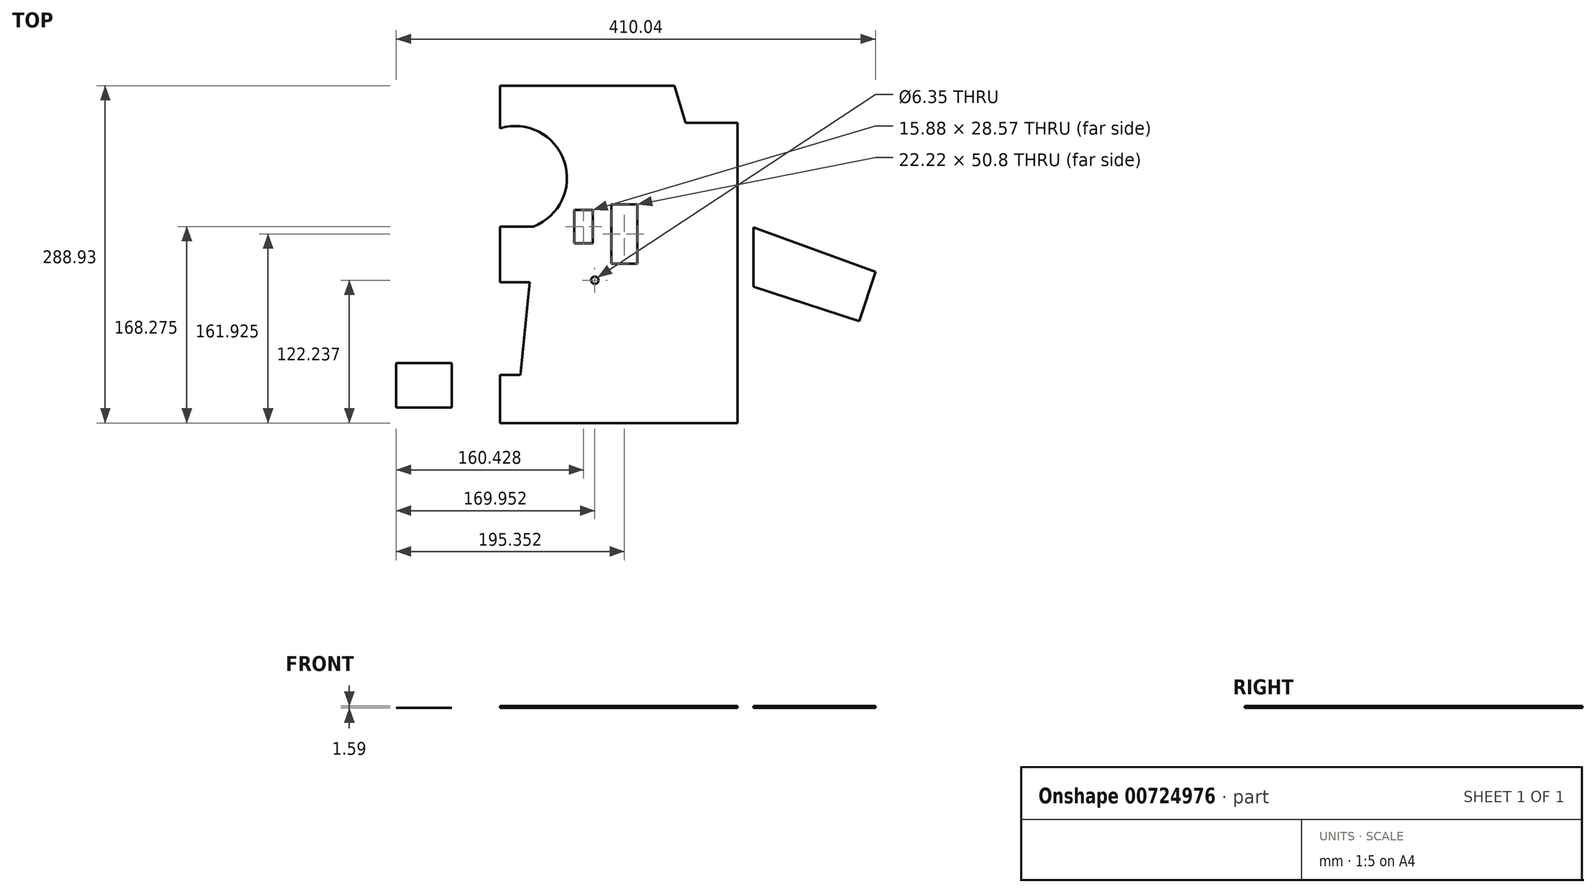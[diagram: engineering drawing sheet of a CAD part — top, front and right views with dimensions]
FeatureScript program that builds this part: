
annotation { "Feature Type Name" : "Feature", "Feature Type Description" : "" }
export const myFeature = defineFeature(function(context is Context, id is Id, definition is map)
    precondition{}
    {
        {
            var Q0;
            Q0=qCreatedBy(makeId("Top.planeOp"),FACE);
            var sketch = newSketch(context, id + "F0", { "sketchPlane" : qUnion([Q0])});
            skLineSegment(sketch, "E0.bottom", {"start": v(0, 0) * mm, "end": v(203.2, 0) * mm, "construction": true});
            skLineSegment(sketch, "E0.top", {"start": v(0, 288.93) * mm, "end": v(203.2, 288.93) * mm, "construction": true});
            skLineSegment(sketch, "E0.left", {"start": v(0, 0) * mm, "end": v(0, 288.93) * mm, "construction": true});
            skLineSegment(sketch, "E0.right", {"start": v(203.2, 0) * mm, "end": v(203.2, 288.93) * mm, "construction": true});
            skLineSegment(sketch, "E1", {"start": v(203.2, 0) * mm, "end": v(203.2, 257.18) * mm});
            skLineSegment(sketch, "E2", {"start": v(203.2, 257.18) * mm, "end": v(158.75, 257.18) * mm});
            skLineSegment(sketch, "E3", {"start": v(158.75, 257.18) * mm, "end": v(149.22, 288.93) * mm});
            skLineSegment(sketch, "E4", {"start": v(149.22, 288.93) * mm, "end": v(0, 288.93) * mm});
            skLineSegment(sketch, "E5", {"start": v(0, 288.93) * mm, "end": v(0, 252.41) * mm});
            skLineSegment(sketch, "E6", {"start": v(203.2, 0) * mm, "end": v(0, 0) * mm});
            skLineSegment(sketch, "E7", {"start": v(0, 41.28) * mm, "end": v(17.46, 41.28) * mm});
            skLineSegment(sketch, "E8", {"start": v(17.46, 41.28) * mm, "end": v(25.4, 120.65) * mm});
            skLineSegment(sketch, "E9", {"start": v(25.4, 120.65) * mm, "end": v(0, 120.65) * mm});
            skLineSegment(sketch, "E10", {"start": v(0, 0) * mm, "end": v(0, 41.28) * mm});
            skLineSegment(sketch, "E11", {"start": v(0, 168.28) * mm, "end": v(203.2, 168.28) * mm, "construction": true});
            skLineSegment(sketch, "E12", {"start": v(0, 117.48) * mm, "end": v(203.2, 117.48) * mm, "construction": true});
            skArc(sketch, "E13", {"start": v(28.52, 168.28) * mm, "mid": v(54.8, 224.08) * mm, "end": v(0, 252.41) * mm});
            skLineSegment(sketch, "E14", {"start": v(28.52, 168.28) * mm, "end": v(0, 168.28) * mm});
            skLineSegment(sketch, "E15", {"start": v(0, 168.28) * mm, "end": v(0, 120.65) * mm});
            skLineSegment(sketch, "E16", {"start": v(216.7, 167.58) * mm, "end": v(216.7, 116.78) * mm});
            skLineSegment(sketch, "E17", {"start": v(216.7, 116.78) * mm, "end": v(307.22, 87.14) * mm});
            skLineSegment(sketch, "E18", {"start": v(307.22, 87.14) * mm, "end": v(321.05, 129.38) * mm});
            skLineSegment(sketch, "E19", {"start": v(321.05, 129.38) * mm, "end": v(216.7, 167.58) * mm});
            skLineSegment(sketch, "E20.bottom", {"start": v(63.5, 182.56) * mm, "end": v(79.38, 182.56) * mm});
            skLineSegment(sketch, "E20.top", {"start": v(63.5, 153.99) * mm, "end": v(79.38, 153.99) * mm});
            skLineSegment(sketch, "E20.left", {"start": v(63.5, 182.56) * mm, "end": v(63.5, 153.99) * mm});
            skLineSegment(sketch, "E20.right", {"start": v(79.38, 182.56) * mm, "end": v(79.38, 153.99) * mm});
            skLineSegment(sketch, "E21.bottom", {"start": v(95.25, 187.33) * mm, "end": v(117.48, 187.33) * mm});
            skLineSegment(sketch, "E21.top", {"start": v(95.25, 136.53) * mm, "end": v(117.48, 136.53) * mm});
            skLineSegment(sketch, "E21.left", {"start": v(95.25, 187.33) * mm, "end": v(95.25, 136.53) * mm});
            skLineSegment(sketch, "E21.right", {"start": v(117.48, 187.33) * mm, "end": v(117.48, 136.53) * mm});
            skPoint(sketch, "E22", {"position": v(63.5, 168.28) * mm});
            skCircle(sketch, "E23", {"center": v(80.96, 122.24) * mm, "radius": 3.18 * mm});
            skLineSegment(sketch, "E24.bottom", {"start": v(-88.99, 51.26) * mm, "end": v(-41.36, 51.26) * mm});
            skLineSegment(sketch, "E24.top", {"start": v(-88.99, 13.16) * mm, "end": v(-41.36, 13.16) * mm});
            skLineSegment(sketch, "E24.left", {"start": v(-88.99, 51.26) * mm, "end": v(-88.99, 13.16) * mm});
            skLineSegment(sketch, "E24.right", {"start": v(-41.36, 51.26) * mm, "end": v(-41.36, 13.16) * mm});
            skLineSegment(sketch, "E25", {"start": v(-88.99, 41.32) * mm, "end": v(-41.36, 41.32) * mm, "construction": true});
            skSolve(sketch);
        }
        {
            var Q0;
            Q0=makeQuery(id+"F0.imprint","IMPRINT",FACE,{"disambiguationData":[TD([[makeQuery(id+"F0.imprint","IMPRINT",EDGE,{"derivedFrom":sQuery(id+"F0.wireOp",EDGE,"E1")}),1.0]])]});
            extrude(context, id + "F1", {"entities" : qUnion([Q0]), "depth" : 1.59 * mm, "offsetDistance" : 25.4 * mm});
        }
        {
            var Q0;
            Q0=makeQuery(id+"F0.imprint","IMPRINT",FACE,{"disambiguationData":[TD([[makeQuery(id+"F0.imprint","IMPRINT",EDGE,{"derivedFrom":sQuery(id+"F0.wireOp",EDGE,"E16")}),1.0]])]});
            extrude(context, id + "F2", {"entities" : qUnion([Q0]), "depth" : 1.59 * mm, "offsetDistance" : 25.4 * mm});
        }
        {
            var Q0;
            Q0=makeQuery(id+"F0.imprint","IMPRINT",FACE,{"disambiguationData":[TD([[makeQuery(id+"F0.imprint","IMPRINT",EDGE,{"derivedFrom":sQuery(id+"F0.wireOp",EDGE,"E24.bottom")}),-1.0]])]});
            extrude(context, id + "F3", {"entities" : qUnion([Q0]), "depth" : 1 / 406.4 * mm, "offsetDistance" : 25.4 * mm});
        }
    });
